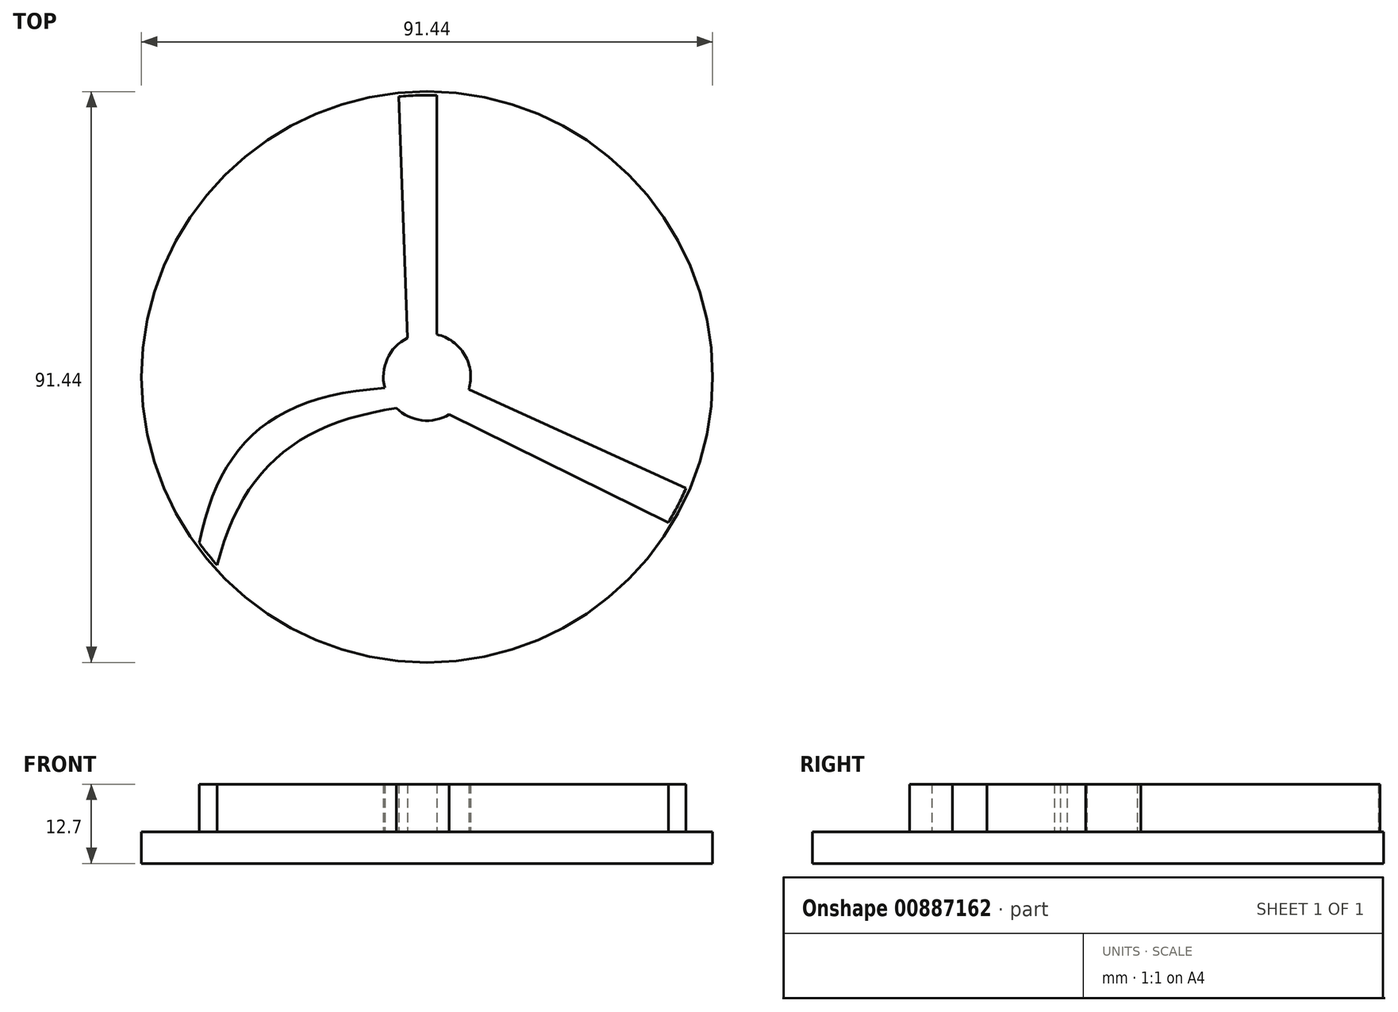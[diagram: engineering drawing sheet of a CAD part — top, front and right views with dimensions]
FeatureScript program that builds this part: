
annotation { "Feature Type Name" : "Feature", "Feature Type Description" : "" }
export const myFeature = defineFeature(function(context is Context, id is Id, definition is map)
    precondition{}
    {
        {
            var Q0;
            Q0=qCreatedBy(makeId("Top.planeOp"),FACE);
            var sketch = newSketch(context, id + "F0", { "sketchPlane" : qUnion([Q0])});
            skCircle(sketch, "E0", {"center": v(0, 0) * mm, "radius": 7 * mm});
            skCircle(sketch, "E1", {"center": v(0, 0) * mm, "radius": 45.14 * mm});
            skLineSegment(sketch, "E2", {"start": v(6.7, -2) * mm, "end": v(41.47, -17.8) * mm});
            skLineSegment(sketch, "E3", {"start": v(3.56, -6.02) * mm, "end": v(38.65, -23.3) * mm});
            skLineSegment(sketch, "E4", {"start": v(1.55, 6.82) * mm, "end": v(1.55, 45.1) * mm});
            skLineSegment(sketch, "E5", {"start": v(-3.12, 6.26) * mm, "end": v(-4.55, 44.9) * mm});
            skFitSpline(sketch, "E6", {"points": [v(-6.77, -1.77) * mm, v(-36.47, -26.6) * mm], "startDerivative": vector(-55.52, -3.63) * mm, "endDerivative": vector(-9.53, -46.92) * mm});
            skFitSpline(sketch, "E7", {"points": [v(-4.9, -5) * mm, v(-33.58, -30.16) * mm], "startDerivative": vector(-46.83, -6.95) * mm, "endDerivative": vector(-11.83, -47.11) * mm});
            skSolve(sketch);
        }
        {
            var Q0;
            {var subQ0=sQuery(id+"F0.wireOp",EDGE,"E4");Q0=makeQuery(id+"F0.imprint","IMPRINT",FACE,{"disambiguationData":[TD([[makeQuery(id+"F0.imprint","IMPRINT",EDGE,{"derivedFrom":subQ0}),1.0]])]});}
            var Q1;
            {var subQ0=sQuery(id+"F0.wireOp",EDGE,"E6");Q1=makeQuery(id+"F0.imprint","IMPRINT",FACE,{"disambiguationData":[TD([[makeQuery(id+"F0.imprint","IMPRINT",EDGE,{"derivedFrom":subQ0}),1.0]])]});}
            var Q2;
            {var subQ0=sQuery(id+"F0.wireOp",EDGE,"E2");Q2=makeQuery(id+"F0.imprint","IMPRINT",FACE,{"disambiguationData":[TD([[makeQuery(id+"F0.imprint","IMPRINT",EDGE,{"derivedFrom":subQ0}),-1.0]])]});}
            var Q3;
            {var subQ0=sQuery(id+"F0.wireOp",EDGE,"E0");var subQ5=makeQuery(id+"F0.imprint","INTERSECT",VERTEX,{"derivedFrom":[subQ0,sQuery(id+"F0.wireOp",EDGE,"E4")]});Q3=makeQuery(id+"F0.imprint","IMPRINT",FACE,{"disambiguationData":[TD([[makeQuery(id+"F0.imprint","IMPRINT",EDGE,{"disambiguationData":[TD([[subQ5,-1.0]])],"derivedFrom":subQ0}),1.0]])]});}
            extrude(context, id + "F1", {"entities" : qUnion([Q0, Q1, Q2, Q3]), "depth" : 7.62 * mm, "offsetDistance" : 25.4 * mm});
        }
        {
            var Q0;
            Q0=qCreatedBy(makeId("Top.planeOp"),FACE);
            var sketch = newSketch(context, id + "F2", { "sketchPlane" : qUnion([Q0])});
            skCircle(sketch, "E8", {"center": v(0, 0) * mm, "radius": 45.72 * mm});
            skSolve(sketch);
        }
        {
            var Q0;
            Q0 = qSketchRegion(id + "F2", true);
            extrude(context, id + "F3", {"entities" : qUnion([Q0]), "operationType" : NewBodyOperationType.ADD, "depth" : -5.08 * mm, "offsetDistance" : 25.4 * mm});
        }
    });
